# Revit family: НЕВАТОМ_Шумоглушитель ГТП, Версия 2
name_source: partatom
category: Арматура воздуховодов
revit_build: Autodesk Revit 2017 (Build: 20170118_1100(x64)
units: mm (PartAtom-declared; Revit-internal decimal feet)

## family parameters
Всегда вертикально = Да
На основе рабочей плоскости = Нет
Общий = Нет
При загрузке вырезать с полостями = Нет
Размер круглого соединителя = Использовать диаметр
Тип детали = Вставляется

## types (20) — shared parameters
ADSK_Единица измерения = шт.
ADSK_Завод-изготовитель = НЕВАТОМ
ADSK_Количество = 1
ADSK_Материал = Сталь оцинкованная
ADSK_Материал наименование = Оцинкованная сталь
ADSK_Наименование = Глушитель ГТП
Nevatom_URL = https://t.me
Ключевая пометка = Вентиляция
zero-valued in all types: ADSK_Масса

## per-type parameters (varying)
| type | A | A1 | ADSK_Размер_Высота | ADSK_Размер_Длина | ADSK_Размер_Ширина | B | B1 | L |
| ГТП 300-150-600 | 300 мм | 340 мм | 150 мм | 300 мм | 600 мм | 150 мм | 190 мм | 600 мм |
| ГТП 1000-500-600 | 1000 мм | 1040 мм | 500 мм | 1000 мм | 600 мм | 500 мм | 540 мм | 600 мм |
| ГТП 400-200-600 | 400 мм | 440 мм | 200 мм | 400 мм | 600 мм | 200 мм | 240 мм | 600 мм |
| ГТП 500-250-600 | 500 мм | 540 мм | 250 мм | 500 мм | 600 мм | 250 мм | 290 мм | 600 мм |
| ГТП 500-300-600 | 500 мм | 540 мм | 300 мм | 500 мм | 600 мм | 300 мм | 340 мм | 600 мм |
| ГТП 600-300-600 | 600 мм | 640 мм | 300 мм | 600 мм | 600 мм | 300 мм | 340 мм | 600 мм |
| ГТП 600-350-600 | 600 мм | 640 мм | 350 мм | 600 мм | 600 мм | 350 мм | 390 мм | 600 мм |
| ГТП 700-400-600 | 700 мм | 740 мм | 400 мм | 700 мм | 600 мм | 400 мм | 440 мм | 600 мм |
| ГТП 800-500-600 | 800 мм | 840 мм | 500 мм | 800 мм | 600 мм | 500 мм | 540 мм | 600 мм |
| ГТП 1000-500-900 | 1000 мм | 1040 мм | 500 мм | 1000 мм | 900 мм | 500 мм | 540 мм | 900 мм |
| ГТП 300-150-900 | 300 мм | 340 мм | 150 мм | 300 мм | 900 мм | 150 мм | 190 мм | 900 мм |
| ГТП 400-200-900 | 400 мм | 440 мм | 200 мм | 400 мм | 900 мм | 200 мм | 240 мм | 900 мм |
| ГТП 500-250-900 | 500 мм | 540 мм | 250 мм | 500 мм | 900 мм | 250 мм | 290 мм | 900 мм |
| ГТП 500-300-900 | 500 мм | 540 мм | 300 мм | 500 мм | 900 мм | 300 мм | 340 мм | 900 мм |
| ГТП 600-300-900 | 600 мм | 640 мм | 300 мм | 600 мм | 900 мм | 300 мм | 340 мм | 900 мм |
| ГТП 600-350-900 | 600 мм | 640 мм | 350 мм | 600 мм | 900 мм | 350 мм | 390 мм | 900 мм |
| ГТП 700-400-900 | 700 мм | 740 мм | 400 мм | 700 мм | 900 мм | 400 мм | 440 мм | 900 мм |
| ГТП 800-500-900 | 800 мм | 840 мм | 500 мм | 800 мм | 900 мм | 500 мм | 540 мм | 900 мм |
| ГТП 900-500-600 | 900 мм | 940 мм | 500 мм | 900 мм | 600 мм | 500 мм | 540 мм | 600 мм |
| ГТП 900-500-900 | 900 мм | 940 мм | 500 мм | 900 мм | 900 мм | 500 мм | 540 мм | 900 мм |

note: column(s) folded — value = type name in every type: ADSK_Марка
